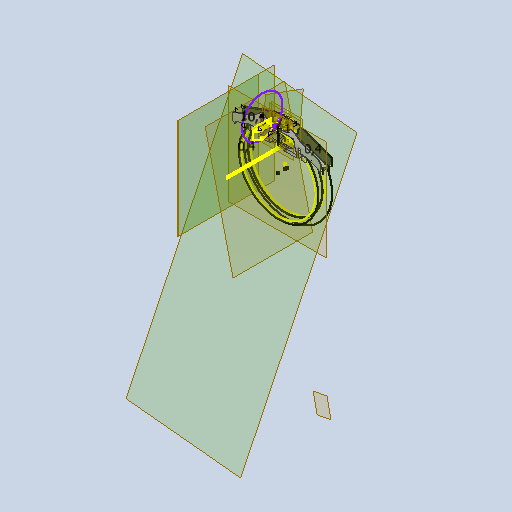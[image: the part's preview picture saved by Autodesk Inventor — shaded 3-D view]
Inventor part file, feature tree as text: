
AUTODESK INVENTOR PART (.ipt)
format: ipt  version: 2022 (Build 260153000, 153)  size: 1,803,776 bytes
history: native  units: mm
features: reference x45, other x40, sketch x31, extrude x25, fillet x22, projected_geometry x21, loft x1, chamfer x1, mirror x1
ambient origin geometry x8: Origin, YZ Plane, XZ Plane, XY Plane, X Axis, Y Axis, Z Axis, Center Point
bodies: Body1 (feature_tree)
feature tree (187):
  other  "Твердое тело2"
  sketch  "Эскиз1"
  other  "РабПлоскость1"
  other  "РабПлоскость2"
  other  "РабПлоскость3"
  sketch  "Эскиз2"
  sketch  "Эскиз3"
  sketch  "Эскиз4"
  other  "РабПлоскость4"
  other  "РабПлоскость5"
  other  "РабПлоскость6"
  sketch  "Эскиз7"
  other  "РабПлоскость7"
  loft  "Лофт2"
  other  "РабПлоскость8"
  extrude  "Выдавливание1"  Depth=1.0mm
  other  "РабПлоскость9"
  extrude  "Выдавливание2"  Depth=1.0mm
  extrude  "Выдавливание3"  Depth=1.0mm
  other  "РабПлоскость10"
  other  "РабПлоскость11"
  extrude  "Выдавливание6"  Depth=0.4mm
  fillet  "Сопряжение2"  Radius=0.4mm
  extrude  "Выдавливание7"  Depth=0.4mm
  other  "РабПлоскость12"
  extrude  "Выдавливание8"  Depth=1.0mm
  extrude  "Выдавливание9"  Depth=1.0mm
  fillet  "Сопряжение6"  Radius=2.0mm
  other  "РабПлоскость13"
  extrude  "Выдавливание10"  TaperAngle=0.0deg  [1 undecoded]
  extrude  "Выдавливание11"  TaperAngle=0.0deg  [1 undecoded]
  extrude  "Выдавливание12"  Depth=2.0mm
  other  "РабПлоскость14"
  extrude  "Выдавливание13"  Depth=1.0mm
  chamfer  "Фаска1"  Distance=40.0mm
  fillet  "Сопряжение7"  Radius=0.2mm
  fillet  "Сопряжение8"  [1 undecoded]
  fillet  "Сопряжение10"  Radius=1.0mm
  fillet  "Сопряжение11"  Radius=1.0mm
  fillet  "Сопряжение12"  Radius=5.0mm
  mirror  "Зеркальное отражение1"
  extrude  "Выдавливание16"  Depth=5.0mm
  other  "РабПлоскость16"
  extrude  "Выдавливание17"  Depth=27.925268mm
  fillet  "Сопряжение13"  Radius=0.25mm
  fillet  "Сопряжение15"  Radius=1.5mm
  fillet  "Сопряжение16"  Radius=17.0mm
  fillet  "Сопряжение17"  Radius=10.0mm
  fillet  "Сопряжение18"  Radius=0.9mm
  extrude  "Выдавливание18"  Depth=0.9mm TaperAngle=0.0deg
  other  "РабПлоскость17"
  extrude  "Выдавливание19"  Depth=0.9mm TaperAngle=0.0deg
  other  "РабПлоскость18"
  extrude  "Выдавливание20"  Depth=1.0mm
  fillet  "Сопряжение19"  Radius=10.0mm
  fillet  "Сопряжение20"  Radius=3.0mm
  extrude  "Выдавливание21"  Depth=10.0mm TaperAngle=0.0deg
  fillet  "Сопряжение21"  Radius=1.0mm
  extrude  "Выдавливание22"  Depth=1.5mm
  sketch  "Эскиз36"
  extrude  "Выдавливание24"  Depth=1.0mm
  extrude  "Выдавливание25"  Depth=10.0mm TaperAngle=0.0deg
  fillet  "Сопряжение22"  Radius=0.8mm
  fillet  "Сопряжение23"  Radius=2.0mm
  extrude  "Выдавливание29"  Depth=1.0mm
  extrude  "Выдавливание30"  Depth=3.0mm
  other  "РабПлоскость19"
  extrude  "Выдавливание31"  Depth=2.0mm
  fillet  "Сопряжение27"  Radius=1.0mm
  extrude  "Выдавливание32"  Depth=3.0mm TaperAngle=0.0deg
  fillet  "Сопряжение28"  Radius=1.5mm
  fillet  "Сопряжение29"  Radius=2.0mm
  fillet  "Сопряжение30"  Radius=2.5mm
  fillet  "Сопряжение32"  Radius=0.5mm
  extrude  "Выдавливание34"  Depth=0.2mm
  reference  "Ссылка1"
  reference  "Ссылка2"
  reference  "Ссылка6"
  reference  "Ссылка7"
  reference  "Ссылка8"
  reference  "Ссылка9"
  reference  "Ссылка10"
  reference  "Ссылка11"
  reference  "Ссылка12"
  reference  "Ссылка13"
  reference  "Ссылка14"
  reference  "Ссылка15"
  reference  "Ссылка16"
  reference  "Ссылка17"
  reference  "Ссылка18"
  reference  "Ссылка19"
  reference  "Ссылка20"
  sketch  "Эскиз8"
  sketch  "Эскиз9"
  reference  "Ссылка21"
  sketch  "Эскиз10"
  projected_geometry  "Спроецированная петля1"
  projected_geometry  "Спроецированная петля2"
  sketch  "Эскиз11"
  projected_geometry  "Спроецированная петля3"
  sketch  "Эскиз14"
  reference  "Ссылка25"
  projected_geometry  "Спроецированная петля4"
  reference  "Ссылка26"
  sketch  "Эскиз16"
  projected_geometry  "Спроецированная петля5"
  projected_geometry  "Спроецированная петля6"
  projected_geometry  "Спроецированная петля7"
  sketch  "Эскиз17"
  sketch  "Эскиз18"
  projected_geometry  "Спроецированная петля8"
  projected_geometry  "Спроецированная петля9"
  sketch  "Эскиз19"
  projected_geometry  "Спроецированная петля10"
  sketch  "Эскиз20"
  projected_geometry  "Спроецированная петля11"
  reference  "Ссылка27"
  sketch  "Эскиз21"
  projected_geometry  "Спроецированная петля12"
  sketch  "Эскиз22"
  reference  "Ссылка28"
  reference  "Ссылка29"
  reference  "Ссылка30"
  sketch  "Эскиз25"
  projected_geometry  "Спроецированная петля13"
  projected_geometry  "Спроецированная петля14"
  reference  "Ссылка31"
  sketch  "Эскиз26"
  reference  "Ссылка32"
  reference  "Ссылка33"
  sketch  "Эскиз27"
  reference  "Ссылка34"
  sketch  "Эскиз28"
  reference  "Ссылка35"
  reference  "Ссылка39"
  sketch  "Эскиз31"
  reference  "Ссылка40"
  reference  "Ссылка41"
  reference  "Ссылка42"
  reference  "Ссылка43"
  sketch  "Эскиз32"
  reference  "Ссылка44"
  sketch  "Эскиз33"
  reference  "Ссылка45"
  sketch  "Эскиз37"
  reference  "Ссылка46"
  projected_geometry  "Спроецированная петля18"
  sketch  "Эскиз38"
  projected_geometry  "Спроецированная петля19"
  sketch  "Эскиз42"
  reference  "Ссылка52"
  reference  "Ссылка53"
  reference  "Ссылка54"
  reference  "Ссылка55"
  sketch  "Эскиз43"
  projected_geometry  "Спроецированная петля21"
  reference  "Ссылка56"
  projected_geometry  "Спроецированная петля22"
  projected_geometry  "Спроецированная петля23"
  sketch  "Эскиз45"
  projected_geometry  "Спроецированная петля24"
  sketch  "Эскиз47"
  projected_geometry  "Спроецированная петля26"
  reference  "Ссылка62"
  reference  "Ссылка63"
  reference  "Ссылка64"
  other  "<userpath>\Documents\Git\MZCAT_2024\MZCAT_2.iam"
  other  "MZCAT_2.iam"
  other  "magazine:1"
  other  "CAT_protector:1"
  other  "plan:1"
  other  "base plate:2"
  other  "<userpath>\Documents\Git\MZCAT_2024\MZCAT_4.iam"
  other  "MZCAT_4.iam"
  other  "vydacha_pusher:2"
  other  "vydacha_pusher:1"
  other  "magazine_fixator:1"
  other  "OCS-D008 B:1"
  other  "<userpath>\Documents\Git\MZCAT_2024\MZCAT_3.iam"
  other  "MZCAT_3.iam"
  other  "lidar_base:1"
  other  "lidar_krestovina_base:1"
  other  "motherboard_plate:1"
  other  "commutationCATboard:1"
  other  "FastBattery:1"
  other  "metal_cap:1"
  other  "cable_slide:1"
note: 3 required parameter values undecoded (feature->parameter linkage not recoverable at this tier; creation-order binding heuristic only, values carry confidence <= 0.55)
